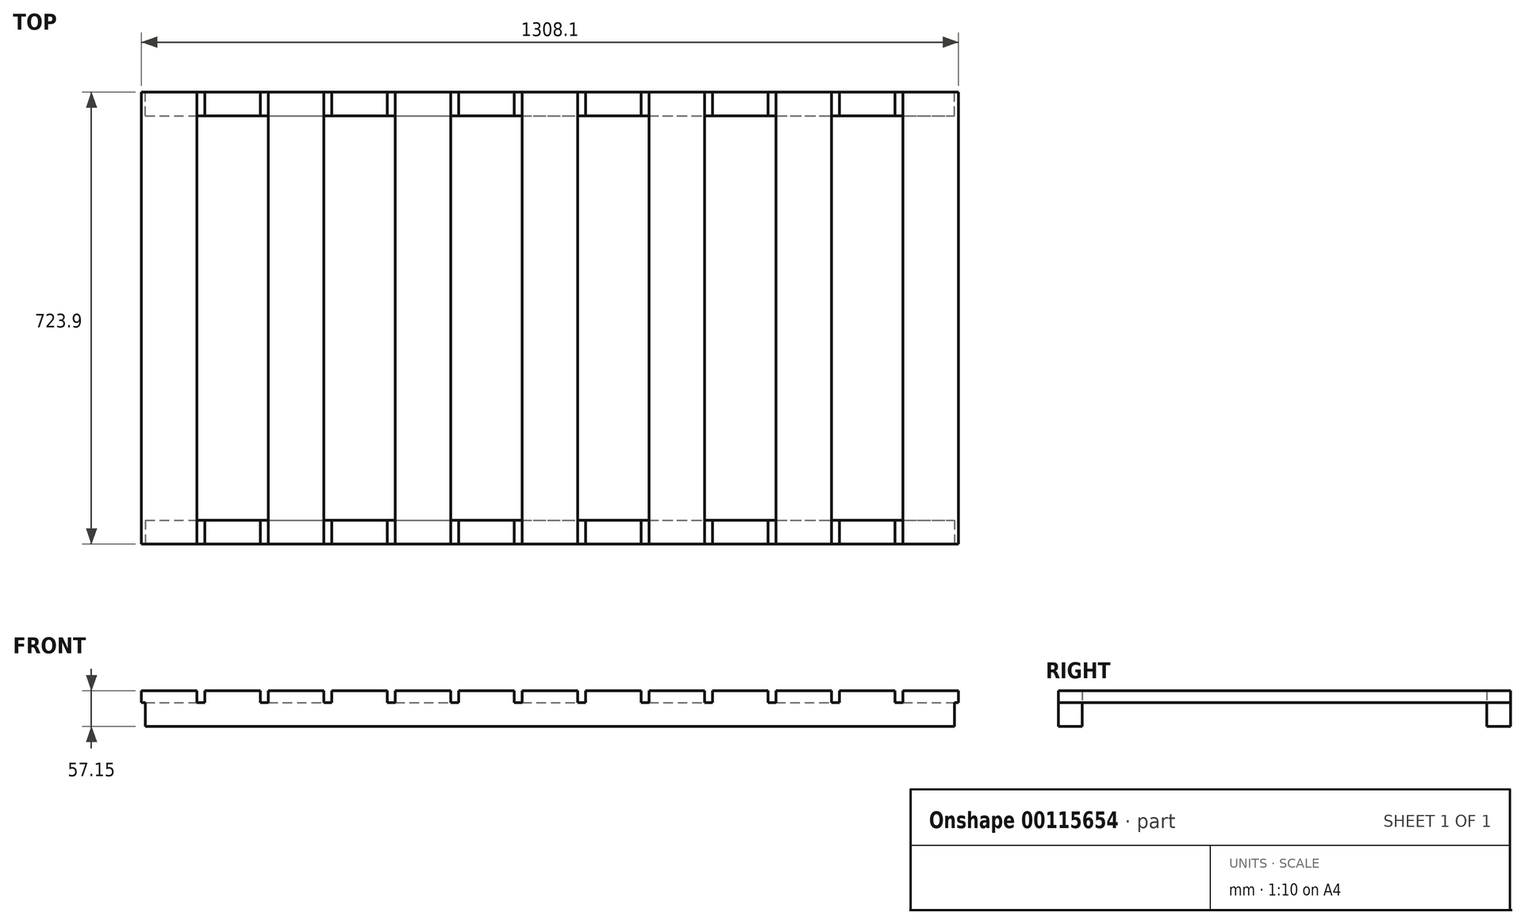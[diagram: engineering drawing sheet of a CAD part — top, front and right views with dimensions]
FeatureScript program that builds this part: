
annotation { "Feature Type Name" : "Feature", "Feature Type Description" : "" }
export const myFeature = defineFeature(function(context is Context, id is Id, definition is map)
    precondition{}
    {
        {
            var Q0;
            Q0=qCreatedBy(makeId("Top.planeOp"),FACE);
            var sketch = newSketch(context, id + "F0", { "sketchPlane" : qUnion([Q0])});
            skLineSegment(sketch, "E0.bottom", {"start": v(0, -323.85) * mm, "end": v(1295.4, -323.85) * mm});
            skLineSegment(sketch, "E0.top", {"start": v(0, -361.95) * mm, "end": v(1295.4, -361.95) * mm});
            skLineSegment(sketch, "E0.left", {"start": v(0, -323.85) * mm, "end": v(0, -361.95) * mm});
            skLineSegment(sketch, "E0.right", {"start": v(1295.4, -323.85) * mm, "end": v(1295.4, -361.95) * mm});
            skLineSegment(sketch, "E1", {"start": v(0, 0) * mm, "end": v(688.43, 0) * mm, "construction": true});
            skSolve(sketch);
        }
        {
            var Q0;
            Q0 = qSketchRegion(id + "F0", true);
            extrude(context, id + "F1", {"entities" : qUnion([Q0]), "depth" : 38.1 * mm});
        }
        {
            var Q0;
            Q0=makeQuery(id+"F1.opExtrude","CAP_FACE",FACE,{"disambiguationData":[OSD([sQuery(id+"F0.wireOp",EDGE,"E0.bottom"),sQuery(id+"F0.wireOp",EDGE,"E0.top"),sQuery(id+"F0.wireOp",EDGE,"E0.left"),sQuery(id+"F0.wireOp",EDGE,"E0.right")])],"isStart":false});
            var sketch = newSketch(context, id + "F2", { "sketchPlane" : qUnion([Q0])});
            skLineSegment(sketch, "E2.bottom", {"start": v(603.25, -361.95) * mm, "end": v(692.15, -361.95) * mm});
            skLineSegment(sketch, "E2.top", {"start": v(603.25, 0) * mm, "end": v(692.15, 0) * mm});
            skLineSegment(sketch, "E2.left", {"start": v(603.25, -361.95) * mm, "end": v(603.25, 0) * mm});
            skLineSegment(sketch, "E2.right", {"start": v(692.15, -361.95) * mm, "end": v(692.15, 0) * mm});
            skPoint(sketch, "E3", {"position": v(647.7, -361.95) * mm});
            skPoint(sketch, "E4.1.0.0", {"position": v(850.9, -361.95) * mm});
            skLineSegment(sketch, "E4.1.0.1", {"start": v(806.45, -361.95) * mm, "end": v(895.35, -361.95) * mm});
            skLineSegment(sketch, "E4.1.0.2", {"start": v(806.45, 0) * mm, "end": v(895.35, 0) * mm});
            skLineSegment(sketch, "E4.1.0.3", {"start": v(806.45, -361.95) * mm, "end": v(806.45, 0) * mm});
            skLineSegment(sketch, "E4.1.0.4", {"start": v(895.35, -361.95) * mm, "end": v(895.35, 0) * mm});
            skPoint(sketch, "E4.2.0.0", {"position": v(1054.1, -361.95) * mm});
            skLineSegment(sketch, "E4.2.0.1", {"start": v(1009.65, -361.95) * mm, "end": v(1098.55, -361.95) * mm});
            skLineSegment(sketch, "E4.2.0.2", {"start": v(1009.65, 0) * mm, "end": v(1098.55, 0) * mm});
            skLineSegment(sketch, "E4.2.0.3", {"start": v(1009.65, -361.95) * mm, "end": v(1009.65, 0) * mm});
            skLineSegment(sketch, "E4.2.0.4", {"start": v(1098.55, -361.95) * mm, "end": v(1098.55, 0) * mm});
            skPoint(sketch, "E4.3.0.0", {"position": v(1257.3, -361.95) * mm});
            skLineSegment(sketch, "E4.3.0.1", {"start": v(1212.85, -361.95) * mm, "end": v(1301.75, -361.95) * mm});
            skLineSegment(sketch, "E4.3.0.2", {"start": v(1212.85, 0) * mm, "end": v(1301.75, 0) * mm});
            skLineSegment(sketch, "E4.3.0.3", {"start": v(1212.85, -361.95) * mm, "end": v(1212.85, 0) * mm});
            skLineSegment(sketch, "E4.3.0.4", {"start": v(1301.75, -361.95) * mm, "end": v(1301.75, 0) * mm});
            skLineSegment(sketch, "E4.direction1", {"start": v(603.25, -361.95) * mm, "end": v(806.45, -361.95) * mm, "construction": true});
            skPoint(sketch, "E5.1.0.0", {"position": v(444.5, -361.95) * mm});
            skLineSegment(sketch, "E5.1.0.1", {"start": v(400.05, 0) * mm, "end": v(488.95, 0) * mm});
            skLineSegment(sketch, "E5.1.0.2", {"start": v(400.05, -361.95) * mm, "end": v(400.05, 0) * mm});
            skLineSegment(sketch, "E5.1.0.3", {"start": v(488.95, -361.95) * mm, "end": v(488.95, 0) * mm});
            skLineSegment(sketch, "E5.1.0.4", {"start": v(400.05, -361.95) * mm, "end": v(488.95, -361.95) * mm});
            skPoint(sketch, "E5.2.0.0", {"position": v(241.3, -361.95) * mm});
            skLineSegment(sketch, "E5.2.0.1", {"start": v(196.85, 0) * mm, "end": v(285.75, 0) * mm});
            skLineSegment(sketch, "E5.2.0.2", {"start": v(196.85, -361.95) * mm, "end": v(196.85, 0) * mm});
            skLineSegment(sketch, "E5.2.0.3", {"start": v(285.75, -361.95) * mm, "end": v(285.75, 0) * mm});
            skLineSegment(sketch, "E5.2.0.4", {"start": v(196.85, -361.95) * mm, "end": v(285.75, -361.95) * mm});
            skPoint(sketch, "E5.3.0.0", {"position": v(38.1, -361.95) * mm});
            skLineSegment(sketch, "E5.3.0.1", {"start": v(-6.35, 0) * mm, "end": v(82.55, 0) * mm});
            skLineSegment(sketch, "E5.3.0.2", {"start": v(-6.35, -361.95) * mm, "end": v(-6.35, 0) * mm});
            skLineSegment(sketch, "E5.3.0.3", {"start": v(82.55, -361.95) * mm, "end": v(82.55, 0) * mm});
            skLineSegment(sketch, "E5.3.0.4", {"start": v(-6.35, -361.95) * mm, "end": v(82.55, -361.95) * mm});
            skLineSegment(sketch, "E5.direction1", {"start": v(603.25, -361.95) * mm, "end": v(400.05, -361.95) * mm, "construction": true});
            skLineSegment(sketch, "E6.bottom", {"start": v(704.85, -323.85) * mm, "end": v(793.75, -323.85) * mm});
            skLineSegment(sketch, "E6.top", {"start": v(704.85, -361.95) * mm, "end": v(793.75, -361.95) * mm});
            skLineSegment(sketch, "E6.left", {"start": v(704.85, -323.85) * mm, "end": v(704.85, -361.95) * mm});
            skLineSegment(sketch, "E6.right", {"start": v(793.75, -323.85) * mm, "end": v(793.75, -361.95) * mm});
            skLineSegment(sketch, "E7", {"start": v(704.85, -323.85) * mm, "end": v(692.15, -323.85) * mm, "construction": true});
            skLineSegment(sketch, "E8", {"start": v(793.75, -323.85) * mm, "end": v(806.45, -323.85) * mm, "construction": true});
            skLineSegment(sketch, "E9.1.0.0", {"start": v(908.05, -361.95) * mm, "end": v(996.95, -361.95) * mm});
            skLineSegment(sketch, "E9.1.0.1", {"start": v(996.95, -323.85) * mm, "end": v(996.95, -361.95) * mm});
            skLineSegment(sketch, "E9.1.0.2", {"start": v(908.05, -323.85) * mm, "end": v(996.95, -323.85) * mm});
            skLineSegment(sketch, "E9.1.0.3", {"start": v(908.05, -323.85) * mm, "end": v(908.05, -361.95) * mm});
            skLineSegment(sketch, "E9.2.0.0", {"start": v(1111.25, -361.95) * mm, "end": v(1200.15, -361.95) * mm});
            skLineSegment(sketch, "E9.2.0.1", {"start": v(1200.15, -323.85) * mm, "end": v(1200.15, -361.95) * mm});
            skLineSegment(sketch, "E9.2.0.2", {"start": v(1111.25, -323.85) * mm, "end": v(1200.15, -323.85) * mm});
            skLineSegment(sketch, "E9.2.0.3", {"start": v(1111.25, -323.85) * mm, "end": v(1111.25, -361.95) * mm});
            skLineSegment(sketch, "E9.direction1", {"start": v(704.85, -361.95) * mm, "end": v(908.05, -361.95) * mm, "construction": true});
            skLineSegment(sketch, "E10.1.0.0", {"start": v(501.65, -323.85) * mm, "end": v(501.65, -361.95) * mm});
            skLineSegment(sketch, "E10.1.0.1", {"start": v(501.65, -323.85) * mm, "end": v(590.55, -323.85) * mm});
            skLineSegment(sketch, "E10.1.0.2", {"start": v(590.55, -323.85) * mm, "end": v(590.55, -361.95) * mm});
            skLineSegment(sketch, "E10.1.0.3", {"start": v(501.65, -361.95) * mm, "end": v(590.55, -361.95) * mm});
            skLineSegment(sketch, "E10.2.0.0", {"start": v(298.45, -323.85) * mm, "end": v(298.45, -361.95) * mm});
            skLineSegment(sketch, "E10.2.0.1", {"start": v(298.45, -323.85) * mm, "end": v(387.35, -323.85) * mm});
            skLineSegment(sketch, "E10.2.0.2", {"start": v(387.35, -323.85) * mm, "end": v(387.35, -361.95) * mm});
            skLineSegment(sketch, "E10.2.0.3", {"start": v(298.45, -361.95) * mm, "end": v(387.35, -361.95) * mm});
            skLineSegment(sketch, "E10.3.0.0", {"start": v(95.25, -323.85) * mm, "end": v(95.25, -361.95) * mm});
            skLineSegment(sketch, "E10.3.0.1", {"start": v(95.25, -323.85) * mm, "end": v(184.15, -323.85) * mm});
            skLineSegment(sketch, "E10.3.0.2", {"start": v(184.15, -323.85) * mm, "end": v(184.15, -361.95) * mm});
            skLineSegment(sketch, "E10.3.0.3", {"start": v(95.25, -361.95) * mm, "end": v(184.15, -361.95) * mm});
            skLineSegment(sketch, "E10.direction1", {"start": v(704.85, -361.95) * mm, "end": v(501.65, -361.95) * mm, "construction": true});
            skSolve(sketch);
        }
        {
            var Q0;
            Q0 = qSketchRegion(id + "F2", true);
            extrude(context, id + "F3", {"entities" : qUnion([Q0]), "operationType" : NewBodyOperationType.ADD, "depth" : 19.05 * mm});
        }
        {
            var Q0;
            Q0=makeQuery(id+"F1.opExtrude","SWEPT_BODY",BODY,{"disambiguationData":[OSD([sQuery(id+"F0.wireOp",EDGE,"E0.bottom"),sQuery(id+"F0.wireOp",EDGE,"E0.top"),sQuery(id+"F0.wireOp",EDGE,"E0.left"),sQuery(id+"F0.wireOp",EDGE,"E0.right")])]});
            var Q1;
            Q1=qCreatedBy(makeId("Front.planeOp"),FACE);
            mirror(context, id + "F4", {"operationType" : NewBodyOperationType.ADD, "entities" : qUnion([Q0]), "mirrorPlane" : qUnion([Q1])});
        }
    });
